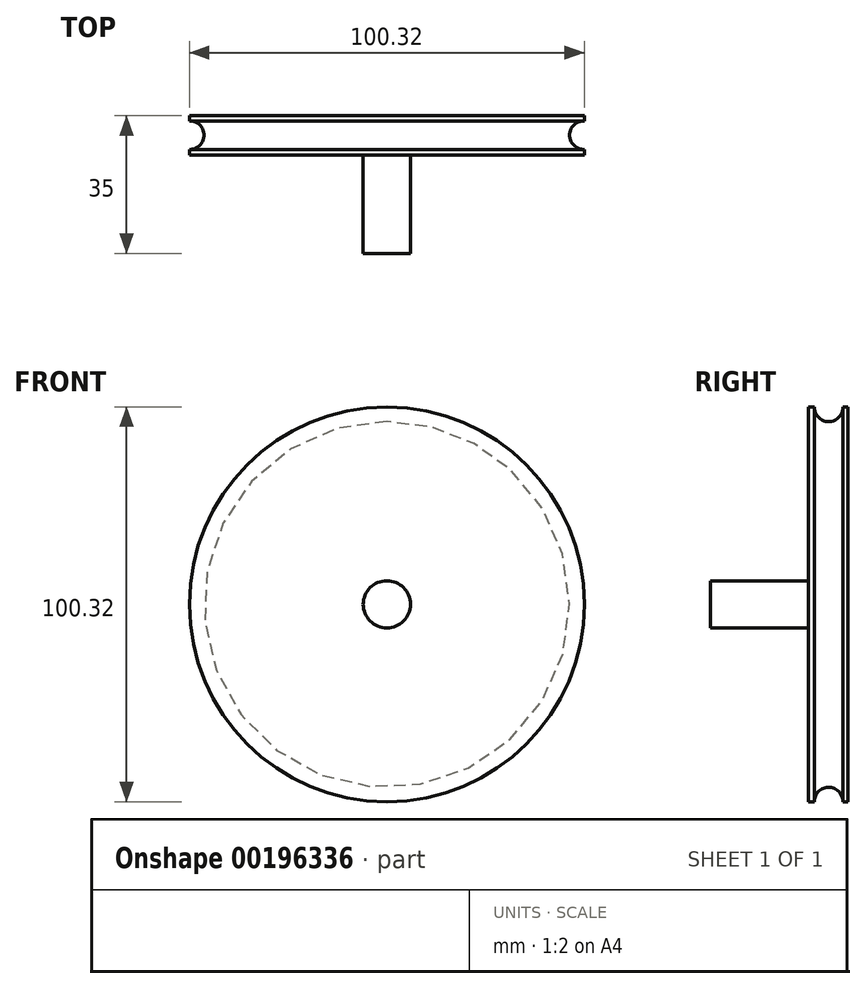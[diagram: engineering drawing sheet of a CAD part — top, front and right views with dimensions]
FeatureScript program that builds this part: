
annotation { "Feature Type Name" : "Feature", "Feature Type Description" : "" }
export const myFeature = defineFeature(function(context is Context, id is Id, definition is map)
    precondition{}
    {
        {
            var Q0;
            Q0=qCreatedBy(makeId("Front.planeOp"),FACE);
            var sketch = newSketch(context, id + "F0", { "sketchPlane" : qUnion([Q0])});
            skCircle(sketch, "E0", {"center": v(0, 0) * mm, "radius": 50.16 * mm});
            skSolve(sketch);
        }
        {
            var Q0;
            Q0 = qSketchRegion(id + "F0", true);
            extrude(context, id + "F1", {"entities" : qUnion([Q0]), "oppositeDirection" : true, "depth" : 10 * mm});
        }
        {
            var Q0;
            Q0=qCreatedBy(makeId("Right.planeOp"),FACE);
            var sketch = newSketch(context, id + "F2", { "sketchPlane" : qUnion([Q0])});
            skPoint(sketch, "E1.end.orphan", {"position": v(0, 50.06) * mm});
            skPoint(sketch, "E2.orphan", {"position": v(0, 0) * mm});
            skLineSegment(sketch, "E3", {"start": v(-24, 0) * mm, "end": v(19.48, 0) * mm});
            skCircle(sketch, "E4", {"center": v(5.05, 50.06) * mm, "radius": 3.63 * mm});
            skPoint(sketch, "E5.trimOffspring.end.orphan", {"position": v(10.1, 50.06) * mm});
            skSolve(sketch);
        }
        {
            var Q0;
            Q0 = qSketchRegion(id + "F2", true);
            var Q1;
            Q1=sQuery(id+"F2.wireOp",EDGE,"E3");
            revolve(context, id + "F3", {"operationType" : NewBodyOperationType.REMOVE, "entities" : qUnion([Q0]), "axis" : qUnion([Q1]), "revolveType" : RevolveType.FULL, "oppositeDirection" : true});
        }
        {
            var Q0;
            Q0=makeQuery(id+"F1.opExtrude","CAP_FACE",FACE,{"disambiguationData":[OSD([sQuery(id+"F0.wireOp",EDGE,"E0")])],"isStart":true});
            var sketch = newSketch(context, id + "F4", { "sketchPlane" : qUnion([Q0])});
            skCircle(sketch, "E6", {"center": v(0, 0) * mm, "radius": 6 * mm});
            skSolve(sketch);
        }
        {
            var Q0;
            Q0 = qSketchRegion(id + "F4", true);
            extrude(context, id + "F5", {"entities" : qUnion([Q0]), "operationType" : NewBodyOperationType.ADD, "depth" : 25 * mm});
        }
        {
            var Q0;
            Q0=qCreatedBy(makeId("Right.planeOp"),FACE);
            var sketch = newSketch(context, id + "F6", { "sketchPlane" : qUnion([Q0])});
            skCircle(sketch, "E7", {"center": v(0, 74.84) * mm, "radius": 3.8 * mm});
            skSolve(sketch);
        }
        {
            var Q0;
            Q0=makeQuery(id+"F6.imprint","IMPRINT",FACE,{"disambiguationData":[TD([[makeQuery(id+"F6.imprint","IMPRINT",EDGE,{"derivedFrom":sQuery(id+"F6.wireOp",EDGE,"E7")}),1.0]])]});
            extrude(context, id + "F7", {"entities" : qUnion([Q0]), "endBound" : BoundingType.SYMMETRIC, "depth" : 200 * mm});
        }
        {
            var Q0;
            Q0=makeQuery(id+"F7.opExtrude","SWEPT_BODY",BODY,{"disambiguationData":[OSD([sQuery(id+"F6.wireOp",EDGE,"E7")])]});
            deleteBodies(context, id + "F8", {"entities" : qUnion([Q0])});
        }
    });
